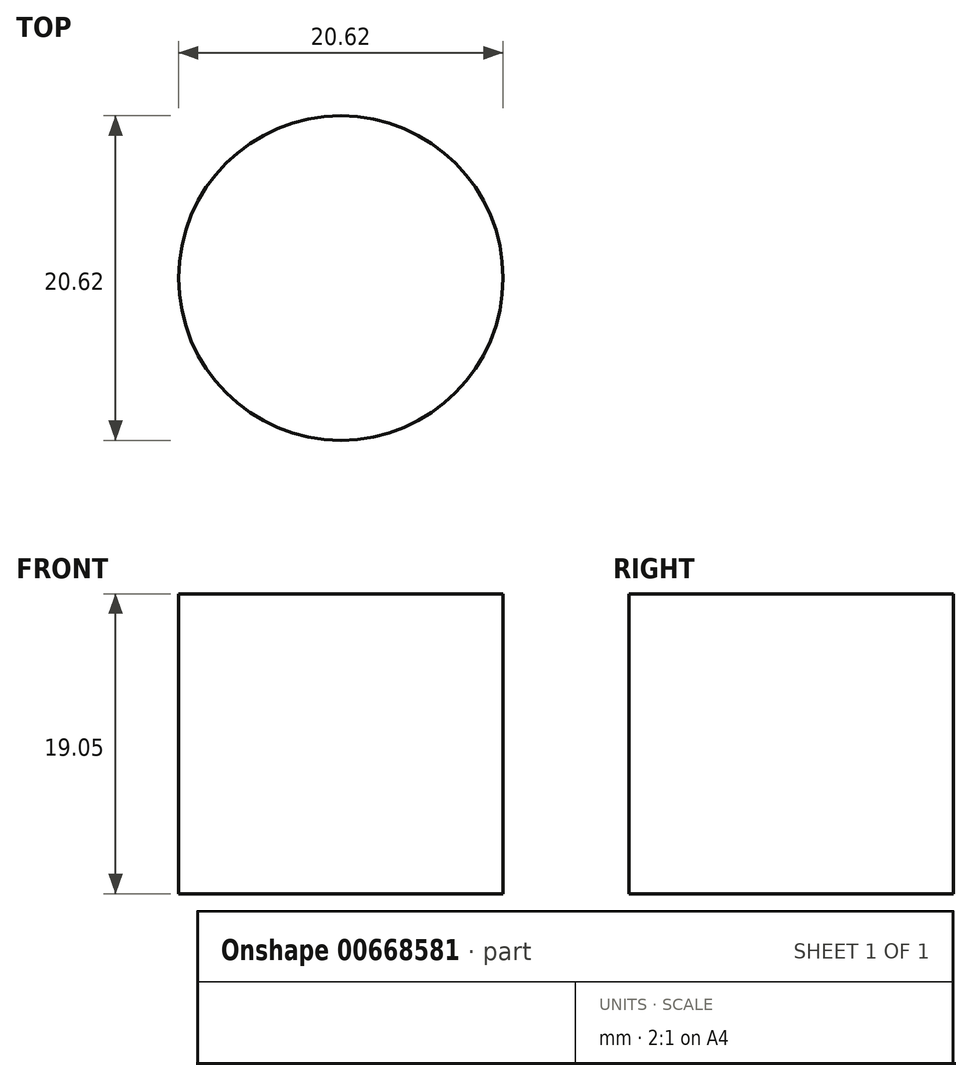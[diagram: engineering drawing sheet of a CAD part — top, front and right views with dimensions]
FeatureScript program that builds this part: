
annotation { "Feature Type Name" : "Feature", "Feature Type Description" : "" }
export const myFeature = defineFeature(function(context is Context, id is Id, definition is map)
    precondition{}
    {
        {
            var Q0;
            Q0=qCreatedBy(makeId("Top.planeOp"),FACE);
            var sketch = newSketch(context, id + "F0", { "sketchPlane" : qUnion([Q0])});
            skCircle(sketch, "E0", {"center": v(0, 0) * mm, "radius": 10.3 * mm});
            skSolve(sketch);
        }
        {
            var Q0;
            Q0=sQuery(id+"F0.wireOp",EDGE,"E0");
            extrude(context, id + "F1", {"bodyType" : ToolBodyType.SURFACE, "surfaceEntities" : qUnion([Q0]), "depth" : 19.05 * mm, "offsetDistance" : 25.4 * mm});
        }
    });
